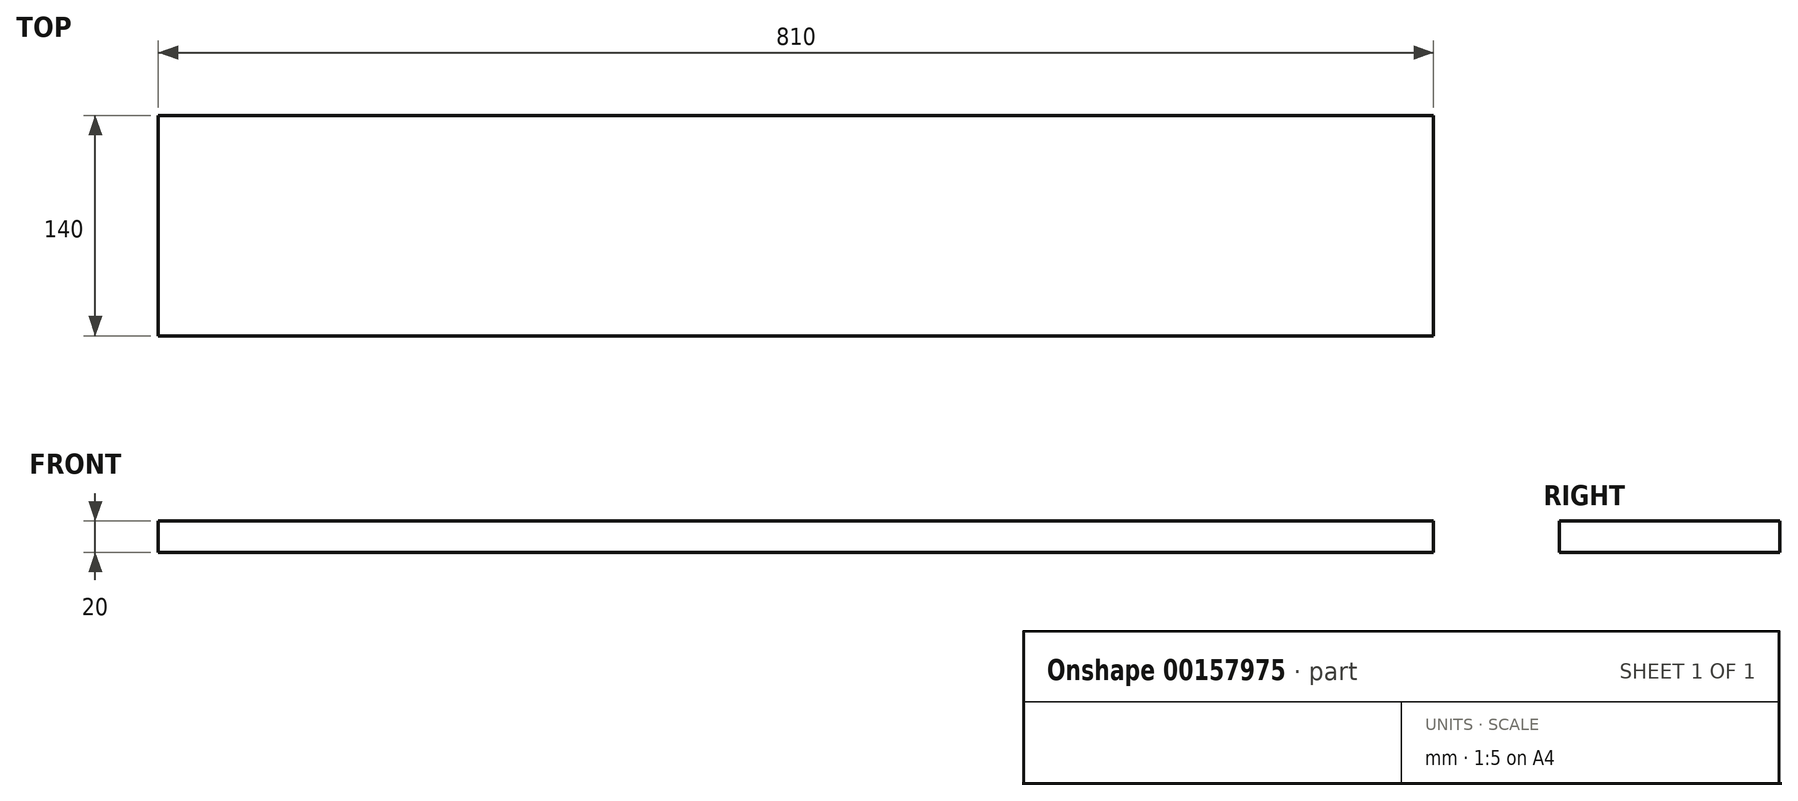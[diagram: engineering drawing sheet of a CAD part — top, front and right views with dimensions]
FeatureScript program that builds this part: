
annotation { "Feature Type Name" : "Feature", "Feature Type Description" : "" }
export const myFeature = defineFeature(function(context is Context, id is Id, definition is map)
    precondition{}
    {
        {
            var Q0;
            Q0=qCreatedBy(makeId("Top.planeOp"),FACE);
            var sketch = newSketch(context, id + "F0", { "sketchPlane" : qUnion([Q0])});
            skLineSegment(sketch, "E0.bottom", {"start": v(-405, -70) * mm, "end": v(405, -70) * mm});
            skLineSegment(sketch, "E0.top", {"start": v(-405, 70) * mm, "end": v(405, 70) * mm});
            skLineSegment(sketch, "E0.left", {"start": v(-405, -70) * mm, "end": v(-405, 70) * mm});
            skLineSegment(sketch, "E0.right", {"start": v(405, -70) * mm, "end": v(405, 70) * mm});
            skPoint(sketch, "E0.middle", {"position": v(0, 0) * mm});
            skSolve(sketch);
        }
        {
            var Q0;
            Q0=qSketchRegion(id+"F0",true);
            extrude(context, id + "F1", {"entities" : qUnion([Q0]), "endBound" : BoundingType.SYMMETRIC, "depth" : 20 * mm});
        }
    });
